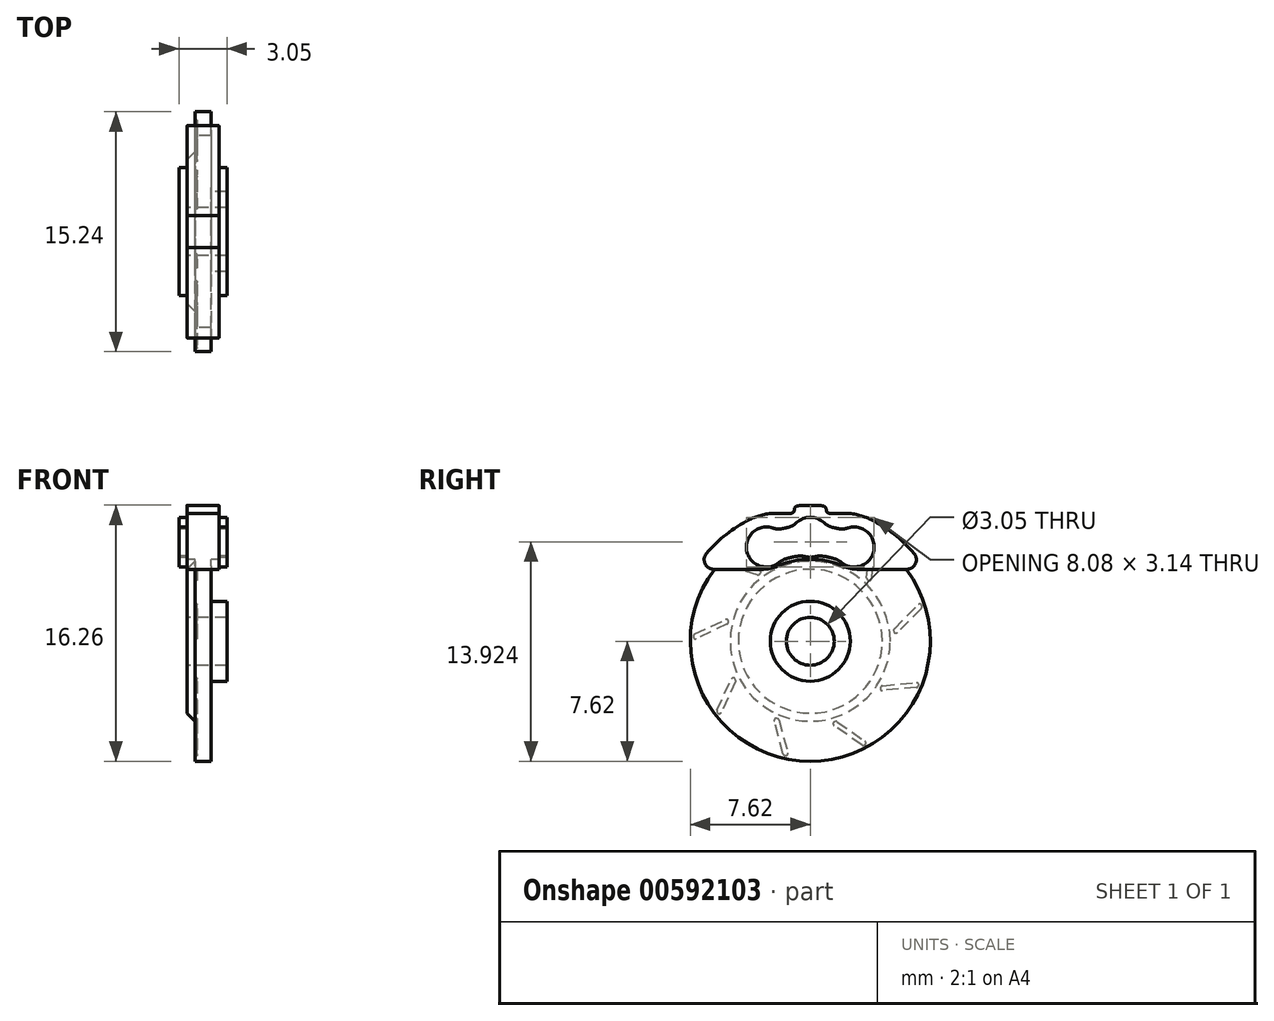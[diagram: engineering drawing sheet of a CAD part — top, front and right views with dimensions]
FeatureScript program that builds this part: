
annotation { "Feature Type Name" : "Feature", "Feature Type Description" : "" }
export const myFeature = defineFeature(function(context is Context, id is Id, definition is map)
    precondition{}
    {
        {
            var Q0;
            Q0=qCreatedBy(makeId("Front.planeOp"),FACE);
            var sketch = newSketch(context, id + "F0", { "sketchPlane" : qUnion([Q0])});
            skLineSegment(sketch, "E0", {"start": v(0, 4.57) * mm, "end": v(0.5, 5.08) * mm});
            skLineSegment(sketch, "E1", {"start": v(0.5, 5.08) * mm, "end": v(0.5, 7.62) * mm});
            skLineSegment(sketch, "E2", {"start": v(0.5, 7.62) * mm, "end": v(1.52, 7.62) * mm});
            skLineSegment(sketch, "E3", {"start": v(1.52, 7.62) * mm, "end": v(1.52, 2.54) * mm});
            skLineSegment(sketch, "E4", {"start": v(1.52, 2.54) * mm, "end": v(2.54, 2.54) * mm});
            skLineSegment(sketch, "E5", {"start": v(2.54, 2.54) * mm, "end": v(2.54, 1.52) * mm});
            skLineSegment(sketch, "E6", {"start": v(2.54, 1.52) * mm, "end": v(0, 1.52) * mm});
            skLineSegment(sketch, "E7", {"start": v(0, 1.52) * mm, "end": v(0, 4.57) * mm});
            skLineSegment(sketch, "E8", {"start": v(0, 0) * mm, "end": v(1.8, 0) * mm});
            skSolve(sketch);
        }
        {
            var Q0;
            Q0 = qSketchRegion(id + "F0", true);
            var Q1;
            Q1=sQuery(id+"F0.wireOp",EDGE,"E8");
            revolve(context, id + "F1", {"entities" : qUnion([Q0]), "axis" : qUnion([Q1]), "revolveType" : RevolveType.FULL});
        }
        {
            var Q0;
            Q0=qCreatedBy(makeId("Right.planeOp"),FACE);
            var sketch = newSketch(context, id + "F2", { "sketchPlane" : qUnion([Q0])});
            skLineSegment(sketch, "E9", {"start": v(0.15, 5.39) * mm, "end": v(-1.1, 7.17) * mm});
            skLineSegment(sketch, "E10", {"start": v(-0.93, 7.37) * mm, "end": v(-1, 7.37) * mm});
            skLineSegment(sketch, "E11", {"start": v(-0.82, 7.31) * mm, "end": v(0.42, 5.53) * mm});
            skLineSegment(sketch, "E12", {"start": v(0.25, 5.33) * mm, "end": v(0.32, 5.33) * mm});
            skPoint(sketch, "E13.visualSharp", {"position": v(-0.86, 7.37) * mm});
            skArc(sketch, "E13.filletArc", {"start": v(-0.82, 7.31) * mm, "mid": v(-0.87, 7.35) * mm, "end": v(-0.93, 7.37) * mm});
            skPoint(sketch, "E14.visualSharp", {"position": v(-1.23, 7.37) * mm});
            skArc(sketch, "E14.filletArc", {"start": v(-1, 7.37) * mm, "mid": v(-1.1, 7.3) * mm, "end": v(-1.1, 7.17) * mm});
            skPoint(sketch, "E15.visualSharp", {"position": v(0.56, 5.33) * mm});
            skArc(sketch, "E15.filletArc", {"start": v(0.32, 5.33) * mm, "mid": v(0.43, 5.4) * mm, "end": v(0.42, 5.53) * mm});
            skPoint(sketch, "E16.visualSharp", {"position": v(0.19, 5.33) * mm});
            skArc(sketch, "E16.filletArc", {"start": v(0.15, 5.39) * mm, "mid": v(0.2, 5.35) * mm, "end": v(0.25, 5.33) * mm});
            skLineSegment(sketch, "E17", {"start": v(0, 0) * mm, "end": v(0.25, 0) * mm});
            skLineSegment(sketch, "E18", {"start": v(0.25, 0) * mm, "end": v(0.25, 5.33) * mm});
            skLineSegment(sketch, "E19.1.0", {"start": v(-5.33, 5.07) * mm, "end": v(-3.24, 4.5) * mm});
            skArc(sketch, "E19.1.1", {"start": v(-3.19, 4.29) * mm, "mid": v(-3.14, 4.41) * mm, "end": v(-3.24, 4.5) * mm});
            skLineSegment(sketch, "E19.1.2", {"start": v(-3.23, 4.25) * mm, "end": v(-3.19, 4.29) * mm});
            skArc(sketch, "E19.1.3", {"start": v(-3.35, 4.22) * mm, "mid": v(-3.29, 4.22) * mm, "end": v(-3.23, 4.25) * mm});
            skLineSegment(sketch, "E19.1.4", {"start": v(-3.35, 4.22) * mm, "end": v(-5.45, 4.79) * mm});
            skArc(sketch, "E19.1.5", {"start": v(-5.5, 5) * mm, "mid": v(-5.54, 4.88) * mm, "end": v(-5.45, 4.79) * mm});
            skArc(sketch, "E19.1.6", {"start": v(-5.33, 5.07) * mm, "mid": v(-5.4, 5.07) * mm, "end": v(-5.45, 5.05) * mm});
            skLineSegment(sketch, "E19.1.7", {"start": v(-5.45, 5.05) * mm, "end": v(-5.5, 5) * mm});
            skLineSegment(sketch, "E19.2.0", {"start": v(-7.34, 0.46) * mm, "end": v(-5.38, 1.37) * mm});
            skArc(sketch, "E19.2.1", {"start": v(-5.2, 1.24) * mm, "mid": v(-5.25, 1.36) * mm, "end": v(-5.38, 1.37) * mm});
            skLineSegment(sketch, "E19.2.2", {"start": v(-5.2, 1.18) * mm, "end": v(-5.2, 1.24) * mm});
            skArc(sketch, "E19.2.3", {"start": v(-5.28, 1.08) * mm, "mid": v(-5.23, 1.12) * mm, "end": v(-5.2, 1.18) * mm});
            skLineSegment(sketch, "E19.2.4", {"start": v(-5.28, 1.08) * mm, "end": v(-7.25, 0.17) * mm});
            skArc(sketch, "E19.2.5", {"start": v(-7.43, 0.3) * mm, "mid": v(-7.38, 0.18) * mm, "end": v(-7.25, 0.17) * mm});
            skArc(sketch, "E19.2.6", {"start": v(-7.34, 0.46) * mm, "mid": v(-7.4, 0.42) * mm, "end": v(-7.42, 0.36) * mm});
            skLineSegment(sketch, "E19.2.7", {"start": v(-7.42, 0.36) * mm, "end": v(-7.43, 0.3) * mm});
            skLineSegment(sketch, "E19.3.0", {"start": v(-5.92, -4.37) * mm, "end": v(-5, -2.4) * mm});
            skArc(sketch, "E19.3.1", {"start": v(-4.78, -2.4) * mm, "mid": v(-4.9, -2.33) * mm, "end": v(-5, -2.4) * mm});
            skLineSegment(sketch, "E19.3.2", {"start": v(-4.75, -2.45) * mm, "end": v(-4.78, -2.4) * mm});
            skArc(sketch, "E19.3.3", {"start": v(-4.74, -2.56) * mm, "mid": v(-4.73, -2.5) * mm, "end": v(-4.75, -2.45) * mm});
            skLineSegment(sketch, "E19.3.4", {"start": v(-4.74, -2.56) * mm, "end": v(-5.66, -4.53) * mm});
            skArc(sketch, "E19.3.5", {"start": v(-5.88, -4.54) * mm, "mid": v(-5.77, -4.6) * mm, "end": v(-5.66, -4.53) * mm});
            skArc(sketch, "E19.3.6", {"start": v(-5.92, -4.37) * mm, "mid": v(-5.93, -4.43) * mm, "end": v(-5.91, -4.49) * mm});
            skLineSegment(sketch, "E19.3.7", {"start": v(-5.91, -4.49) * mm, "end": v(-5.88, -4.54) * mm});
            skLineSegment(sketch, "E19.4.0", {"start": v(-1.73, -7.15) * mm, "end": v(-2.29, -5.06) * mm});
            skArc(sketch, "E19.4.1", {"start": v(-2.12, -4.9) * mm, "mid": v(-2.25, -4.93) * mm, "end": v(-2.29, -5.06) * mm});
            skLineSegment(sketch, "E19.4.2", {"start": v(-2.06, -4.93) * mm, "end": v(-2.12, -4.9) * mm});
            skArc(sketch, "E19.4.3", {"start": v(-1.98, -5.01) * mm, "mid": v(-2.01, -4.96) * mm, "end": v(-2.06, -4.93) * mm});
            skLineSegment(sketch, "E19.4.4", {"start": v(-1.98, -5.01) * mm, "end": v(-1.42, -7.1) * mm});
            skArc(sketch, "E19.4.5", {"start": v(-1.59, -7.26) * mm, "mid": v(-1.46, -7.24) * mm, "end": v(-1.42, -7.1) * mm});
            skArc(sketch, "E19.4.6", {"start": v(-1.73, -7.15) * mm, "mid": v(-1.7, -7.2) * mm, "end": v(-1.65, -7.24) * mm});
            skLineSegment(sketch, "E19.4.7", {"start": v(-1.65, -7.24) * mm, "end": v(-1.59, -7.26) * mm});
            skLineSegment(sketch, "E19.5.0", {"start": v(3.28, -6.59) * mm, "end": v(1.5, -5.34) * mm});
            skArc(sketch, "E19.5.1", {"start": v(1.53, -5.12) * mm, "mid": v(1.44, -5.22) * mm, "end": v(1.5, -5.34) * mm});
            skLineSegment(sketch, "E19.5.2", {"start": v(1.59, -5.1) * mm, "end": v(1.53, -5.12) * mm});
            skArc(sketch, "E19.5.3", {"start": v(1.7, -5.11) * mm, "mid": v(1.65, -5.1) * mm, "end": v(1.59, -5.1) * mm});
            skLineSegment(sketch, "E19.5.4", {"start": v(1.7, -5.11) * mm, "end": v(3.48, -6.36) * mm});
            skArc(sketch, "E19.5.5", {"start": v(3.45, -6.58) * mm, "mid": v(3.53, -6.48) * mm, "end": v(3.48, -6.36) * mm});
            skArc(sketch, "E19.5.6", {"start": v(3.28, -6.59) * mm, "mid": v(3.33, -6.61) * mm, "end": v(3.4, -6.6) * mm});
            skLineSegment(sketch, "E19.5.7", {"start": v(3.4, -6.6) * mm, "end": v(3.45, -6.58) * mm});
            skLineSegment(sketch, "E19.6.0", {"start": v(6.74, -2.94) * mm, "end": v(4.58, -3.13) * mm});
            skArc(sketch, "E19.6.1", {"start": v(4.46, -2.94) * mm, "mid": v(4.46, -3.07) * mm, "end": v(4.58, -3.13) * mm});
            skLineSegment(sketch, "E19.6.2", {"start": v(4.5, -2.89) * mm, "end": v(4.46, -2.94) * mm});
            skArc(sketch, "E19.6.3", {"start": v(4.6, -2.82) * mm, "mid": v(4.53, -2.84) * mm, "end": v(4.5, -2.89) * mm});
            skLineSegment(sketch, "E19.6.4", {"start": v(4.6, -2.82) * mm, "end": v(6.75, -2.63) * mm});
            skArc(sketch, "E19.6.5", {"start": v(6.87, -2.82) * mm, "mid": v(6.87, -2.7) * mm, "end": v(6.75, -2.63) * mm});
            skArc(sketch, "E19.6.6", {"start": v(6.74, -2.94) * mm, "mid": v(6.8, -2.92) * mm, "end": v(6.84, -2.88) * mm});
            skLineSegment(sketch, "E19.6.7", {"start": v(6.84, -2.88) * mm, "end": v(6.87, -2.82) * mm});
            skLineSegment(sketch, "E19.7.0", {"start": v(7.06, 2.08) * mm, "end": v(5.52, 0.55) * mm});
            skArc(sketch, "E19.7.1", {"start": v(5.3, 0.62) * mm, "mid": v(5.4, 0.52) * mm, "end": v(5.52, 0.55) * mm});
            skLineSegment(sketch, "E19.7.2", {"start": v(5.3, 0.68) * mm, "end": v(5.3, 0.62) * mm});
            skArc(sketch, "E19.7.3", {"start": v(5.33, 0.79) * mm, "mid": v(5.3, 0.74) * mm, "end": v(5.3, 0.68) * mm});
            skLineSegment(sketch, "E19.7.4", {"start": v(5.33, 0.79) * mm, "end": v(6.87, 2.32) * mm});
            skArc(sketch, "E19.7.5", {"start": v(7.08, 2.26) * mm, "mid": v(7, 2.35) * mm, "end": v(6.87, 2.32) * mm});
            skArc(sketch, "E19.7.6", {"start": v(7.06, 2.08) * mm, "mid": v(7.09, 2.13) * mm, "end": v(7.1, 2.2) * mm});
            skLineSegment(sketch, "E19.7.7", {"start": v(7.1, 2.2) * mm, "end": v(7.08, 2.26) * mm});
            skLineSegment(sketch, "E19.8.0", {"start": v(4.07, 6.13) * mm, "end": v(3.88, 3.97) * mm});
            skArc(sketch, "E19.8.1", {"start": v(3.67, 3.88) * mm, "mid": v(3.8, 3.86) * mm, "end": v(3.88, 3.97) * mm});
            skLineSegment(sketch, "E19.8.2", {"start": v(3.62, 3.92) * mm, "end": v(3.67, 3.88) * mm});
            skArc(sketch, "E19.8.3", {"start": v(3.58, 4.03) * mm, "mid": v(3.59, 3.97) * mm, "end": v(3.62, 3.92) * mm});
            skLineSegment(sketch, "E19.8.4", {"start": v(3.58, 4.03) * mm, "end": v(3.77, 6.2) * mm});
            skArc(sketch, "E19.8.5", {"start": v(3.98, 6.28) * mm, "mid": v(3.85, 6.3) * mm, "end": v(3.77, 6.2) * mm});
            skArc(sketch, "E19.8.6", {"start": v(4.07, 6.13) * mm, "mid": v(4.06, 6.2) * mm, "end": v(4.02, 6.24) * mm});
            skLineSegment(sketch, "E19.8.7", {"start": v(4.02, 6.24) * mm, "end": v(3.98, 6.28) * mm});
            skPoint(sketch, "E19.center", {"position": v(0, 0) * mm});
            skSolve(sketch);
        }
        {
            var Q0;
            Q0 = qSketchRegion(id + "F2", true);
            extrude(context, id + "F3", {"entities" : qUnion([Q0]), "operationType" : NewBodyOperationType.REMOVE, "depth" : 0.64 * mm, "offsetDistance" : 25.4 * mm});
        }
        {
            var Q0;
            Q0=qCreatedBy(makeId("Right.planeOp"),FACE);
            var sketch = newSketch(context, id + "F4", { "sketchPlane" : qUnion([Q0])});
            skArc(sketch, "E20", {"start": v(6.6, 5.58) * mm, "mid": v(5.34, 6.8) * mm, "end": v(3.86, 7.73) * mm});
            skLineSegment(sketch, "E21", {"start": v(0, 0) * mm, "end": v(0, 4.57) * mm});
            skLineSegment(sketch, "E22", {"start": v(-3.07, 4.57) * mm, "end": v(-6.13, 4.57) * mm});
            skLineSegment(sketch, "E23", {"start": v(3.07, 4.57) * mm, "end": v(6.13, 4.57) * mm});
            skLineSegment(sketch, "E24", {"start": v(0, 4.57) * mm, "end": v(0, 8.13) * mm});
            skLineSegment(sketch, "E25", {"start": v(2.16, 8.13) * mm, "end": v(1.22, 8.13) * mm});
            skPoint(sketch, "E26.orphan", {"position": v(3.74, 8.13) * mm});
            skLineSegment(sketch, "E27", {"start": v(1.02, 8.33) * mm, "end": v(1.02, 8.35) * mm});
            skLineSegment(sketch, "E28", {"start": v(-1.02, 8.33) * mm, "end": v(-1.02, 8.35) * mm});
            skArc(sketch, "E29.trimOffspring", {"start": v(-3.86, 7.73) * mm, "mid": v(-5.34, 6.8) * mm, "end": v(-6.6, 5.58) * mm});
            skArc(sketch, "E30.trimOffspring", {"start": v(0.79, 8.6) * mm, "mid": v(0, 8.64) * mm, "end": v(-0.79, 8.6) * mm});
            skLineSegment(sketch, "E31.trimOffspring", {"start": v(-1.22, 8.13) * mm, "end": v(-2.16, 8.13) * mm});
            skPoint(sketch, "E32.visualSharp", {"position": v(1.02, 8.58) * mm});
            skArc(sketch, "E32.filletArc", {"start": v(1.02, 8.35) * mm, "mid": v(0.95, 8.52) * mm, "end": v(0.79, 8.6) * mm});
            skPoint(sketch, "E33.visualSharp", {"position": v(-1.02, 8.58) * mm});
            skArc(sketch, "E33.filletArc", {"start": v(-0.79, 8.6) * mm, "mid": v(-0.95, 8.52) * mm, "end": v(-1.02, 8.35) * mm});
            skPoint(sketch, "E34.visualSharp", {"position": v(-1.02, 8.13) * mm});
            skArc(sketch, "E34.filletArc", {"start": v(-1.22, 8.13) * mm, "mid": v(-1.08, 8.19) * mm, "end": v(-1.02, 8.33) * mm});
            skPoint(sketch, "E35.visualSharp", {"position": v(1.02, 8.13) * mm});
            skArc(sketch, "E35.filletArc", {"start": v(1.02, 8.33) * mm, "mid": v(1.08, 8.19) * mm, "end": v(1.22, 8.13) * mm});
            skPoint(sketch, "E36.visualSharp", {"position": v(2.92, 8.13) * mm});
            skArc(sketch, "E36.filletArc", {"start": v(3.86, 7.73) * mm, "mid": v(3.03, 8.03) * mm, "end": v(2.16, 8.13) * mm});
            skPoint(sketch, "E37.visualSharp", {"position": v(-2.92, 8.13) * mm});
            skArc(sketch, "E37.filletArc", {"start": v(-2.16, 8.13) * mm, "mid": v(-3.03, 8.03) * mm, "end": v(-3.86, 7.73) * mm});
            skPoint(sketch, "E38.visualSharp", {"position": v(-7.33, 4.57) * mm});
            skArc(sketch, "E38.filletArc", {"start": v(-6.6, 5.58) * mm, "mid": v(-6.68, 4.92) * mm, "end": v(-6.13, 4.57) * mm});
            skPoint(sketch, "E39.visualSharp", {"position": v(7.33, 4.57) * mm});
            skArc(sketch, "E39.filletArc", {"start": v(6.13, 4.57) * mm, "mid": v(6.68, 4.92) * mm, "end": v(6.6, 5.58) * mm});
            skArc(sketch, "E40", {"start": v(2.06, 4.78) * mm, "mid": v(0, 5.2) * mm, "end": v(-2.06, 4.78) * mm});
            skPoint(sketch, "E41.visualSharp", {"position": v(-2.5, 4.57) * mm});
            skArc(sketch, "E41.filletArc", {"start": v(-3.07, 4.57) * mm, "mid": v(-2.56, 4.62) * mm, "end": v(-2.06, 4.78) * mm});
            skPoint(sketch, "E42.visualSharp", {"position": v(2.5, 4.57) * mm});
            skArc(sketch, "E42.filletArc", {"start": v(2.06, 4.78) * mm, "mid": v(2.56, 4.62) * mm, "end": v(3.07, 4.57) * mm});
            skSolve(sketch);
        }
        {
            var Q0;
            Q0 = qSketchRegion(id + "F4", true);
            extrude(context, id + "F5", {"entities" : qUnion([Q0]), "operationType" : NewBodyOperationType.ADD, "depth" : 2.03 * mm, "offsetDistance" : 25.4 * mm});
        }
        {
            var Q0;
            Q0=qCreatedBy(makeId("Right.planeOp"),FACE);
            var sketch = newSketch(context, id + "F6", { "sketchPlane" : qUnion([Q0])});
            skArc(sketch, "E43", {"start": v(-0.32, 5.37) * mm, "mid": v(0, 5.33) * mm, "end": v(0.32, 5.37) * mm});
            skArc(sketch, "E44", {"start": v(1.99, 5) * mm, "mid": v(4.04, 5.75) * mm, "end": v(2.4, 7.2) * mm});
            skLineSegment(sketch, "E45", {"start": v(0, 0) * mm, "end": v(0, 4.22) * mm});
            skLineSegment(sketch, "E46", {"start": v(2.8, 5.99) * mm, "end": v(0, 0) * mm});
            skArc(sketch, "E47.MirrorC", {"start": v(-1.99, 5) * mm, "mid": v(-4.04, 5.75) * mm, "end": v(-2.4, 7.2) * mm});
            skArc(sketch, "E48", {"start": v(1.7, 7.16) * mm, "mid": v(1.6, 7.2) * mm, "end": v(1.48, 7.22) * mm});
            skArc(sketch, "E49.trimOffspring", {"start": v(-0.82, 5.4) * mm, "mid": v(-1.18, 5.33) * mm, "end": v(-1.54, 5.24) * mm});
            skArc(sketch, "E50.trimOffspring", {"start": v(1.54, 5.24) * mm, "mid": v(1.18, 5.33) * mm, "end": v(0.82, 5.4) * mm});
            skArc(sketch, "E51.trimOffspring", {"start": v(-1.48, 7.22) * mm, "mid": v(-1.6, 7.2) * mm, "end": v(-1.7, 7.16) * mm});
            skArc(sketch, "E52.trimOffspring", {"start": v(0.87, 7.53) * mm, "mid": v(0, 7.87) * mm, "end": v(-0.87, 7.53) * mm});
            skPoint(sketch, "E53.visualSharp", {"position": v(-2.11, 7.06) * mm});
            skArc(sketch, "E53.filletArc", {"start": v(-2.4, 7.2) * mm, "mid": v(-2.06, 7.13) * mm, "end": v(-1.7, 7.16) * mm});
            skPoint(sketch, "E54.visualSharp", {"position": v(-1.07, 7.29) * mm});
            skArc(sketch, "E54.filletArc", {"start": v(-1.48, 7.22) * mm, "mid": v(-1.15, 7.33) * mm, "end": v(-0.87, 7.53) * mm});
            skPoint(sketch, "E55.visualSharp", {"position": v(1.07, 7.29) * mm});
            skArc(sketch, "E55.filletArc", {"start": v(0.87, 7.53) * mm, "mid": v(1.15, 7.33) * mm, "end": v(1.48, 7.22) * mm});
            skPoint(sketch, "E56.visualSharp", {"position": v(2.11, 7.06) * mm});
            skArc(sketch, "E56.filletArc", {"start": v(1.7, 7.16) * mm, "mid": v(2.06, 7.13) * mm, "end": v(2.4, 7.2) * mm});
            skPoint(sketch, "E57.visualSharp", {"position": v(1.84, 5.14) * mm});
            skArc(sketch, "E57.filletArc", {"start": v(1.99, 5) * mm, "mid": v(1.77, 5.14) * mm, "end": v(1.54, 5.24) * mm});
            skPoint(sketch, "E58.visualSharp", {"position": v(0.5, 5.44) * mm});
            skArc(sketch, "E58.filletArc", {"start": v(0.82, 5.4) * mm, "mid": v(0.57, 5.41) * mm, "end": v(0.32, 5.37) * mm});
            skPoint(sketch, "E59.visualSharp", {"position": v(-0.5, 5.44) * mm});
            skArc(sketch, "E59.filletArc", {"start": v(-0.32, 5.37) * mm, "mid": v(-0.57, 5.41) * mm, "end": v(-0.82, 5.4) * mm});
            skPoint(sketch, "E60.visualSharp", {"position": v(-1.84, 5.14) * mm});
            skArc(sketch, "E60.filletArc", {"start": v(-1.54, 5.24) * mm, "mid": v(-1.77, 5.14) * mm, "end": v(-1.99, 5) * mm});
            skSolve(sketch);
        }
        {
            var Q0;
            Q0 = qSketchRegion(id + "F6", true);
            extrude(context, id + "F7", {"entities" : qUnion([Q0]), "operationType" : NewBodyOperationType.ADD, "depth" : 2.54 * mm, "offsetDistance" : 25.4 * mm, "hasSecondDirection" : true, "secondDirectionOppositeDirection" : true, "secondDirectionDepth" : 0.5 * mm});
        }
    });
